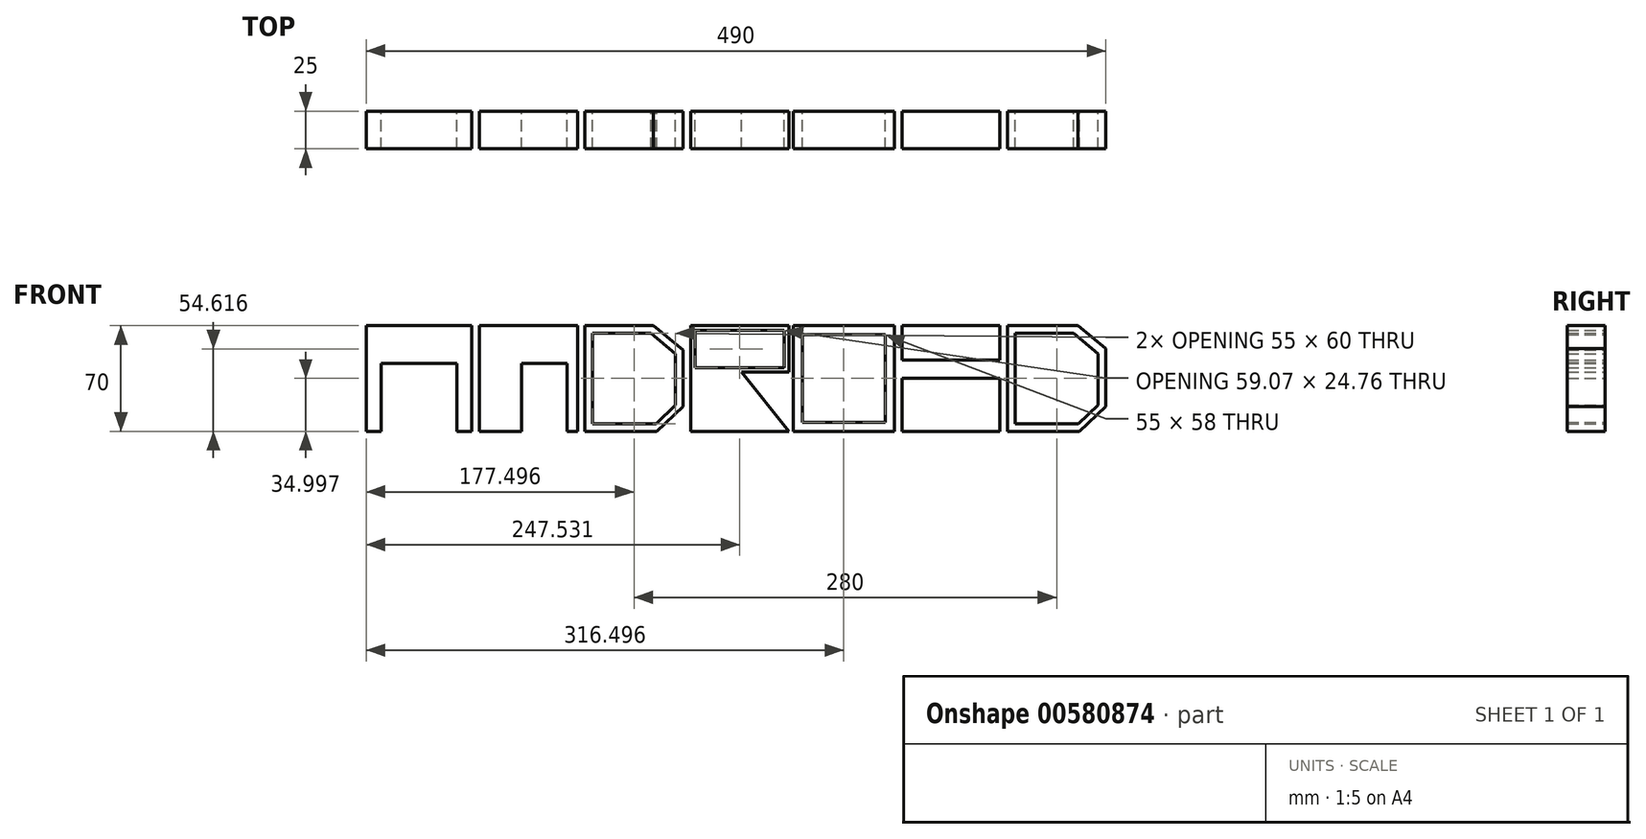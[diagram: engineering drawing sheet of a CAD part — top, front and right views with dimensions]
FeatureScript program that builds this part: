
annotation { "Feature Type Name" : "Feature", "Feature Type Description" : "" }
export const myFeature = defineFeature(function(context is Context, id is Id, definition is map)
    precondition{}
    {
        {
            var Q0;
            Q0=qCreatedBy(makeId("Front.planeOp"),FACE);
            var sketch = newSketch(context, id + "F0", { "sketchPlane" : qUnion([Q0])});
            skLineSegment(sketch, "E0.bottom", {"start": v(-253.98, -12.91) * mm, "end": v(-183.98, -12.91) * mm});
            skLineSegment(sketch, "E0.top", {"start": v(-253.98, -82.91) * mm, "end": v(-243.98, -82.91) * mm});
            skLineSegment(sketch, "E0.left", {"start": v(-253.98, -12.91) * mm, "end": v(-253.98, -82.91) * mm});
            skLineSegment(sketch, "E0.right", {"start": v(236.02, -28.1) * mm, "end": v(236.02, -66.45) * mm});
            skLineSegment(sketch, "E1.right", {"start": v(-183.98, -12.91) * mm, "end": v(-183.98, -82.91) * mm});
            skLineSegment(sketch, "E2.bottom", {"start": v(-178.98, -12.91) * mm, "end": v(-113.98, -12.91) * mm});
            skLineSegment(sketch, "E2.top", {"start": v(-178.98, -82.91) * mm, "end": v(-150.98, -82.91) * mm});
            skLineSegment(sketch, "E2.right", {"start": v(-113.98, -12.91) * mm, "end": v(-113.98, -82.91) * mm});
            skLineSegment(sketch, "E3.bottom", {"start": v(-108.98, -12.91) * mm, "end": v(-63.52, -12.91) * mm});
            skLineSegment(sketch, "E3.top", {"start": v(-108.98, -82.91) * mm, "end": v(-61.53, -82.91) * mm});
            skLineSegment(sketch, "E3.right", {"start": v(-43.98, -29.02) * mm, "end": v(-43.98, -66.45) * mm});
            skLineSegment(sketch, "E4.bottom", {"start": v(-38.98, -12.91) * mm, "end": v(26.02, -12.91) * mm});
            skLineSegment(sketch, "E4.top", {"start": v(-38.98, -82.91) * mm, "end": v(26.02, -82.91) * mm});
            skLineSegment(sketch, "E4.right", {"start": v(26.02, -12.91) * mm, "end": v(26.02, -43.67) * mm});
            skLineSegment(sketch, "E5.bottom", {"start": v(29.02, -12.91) * mm, "end": v(96.02, -12.91) * mm});
            skLineSegment(sketch, "E5.top", {"start": v(29.02, -82.91) * mm, "end": v(96.02, -82.91) * mm});
            skLineSegment(sketch, "E5.right", {"start": v(96.02, -12.91) * mm, "end": v(96.02, -82.91) * mm});
            skLineSegment(sketch, "E6.bottom", {"start": v(101.02, -12.91) * mm, "end": v(166.02, -12.91) * mm});
            skLineSegment(sketch, "E6.top", {"start": v(101.02, -82.91) * mm, "end": v(166.02, -82.91) * mm});
            skLineSegment(sketch, "E6.right", {"start": v(166.02, -12.91) * mm, "end": v(166.02, -35.66) * mm});
            skLineSegment(sketch, "E7", {"start": v(-243.98, -82.91) * mm, "end": v(-243.98, -37.91) * mm});
            skLineSegment(sketch, "E8", {"start": v(-243.98, -37.91) * mm, "end": v(-193.98, -37.91) * mm});
            skLineSegment(sketch, "E9", {"start": v(-193.98, -37.91) * mm, "end": v(-193.98, -82.91) * mm});
            skLineSegment(sketch, "E10", {"start": v(-193.98, -82.91) * mm, "end": v(-183.98, -82.91) * mm});
            skLineSegment(sketch, "E11.right", {"start": v(-178.98, -12.91) * mm, "end": v(-178.98, -82.91) * mm});
            skLineSegment(sketch, "E12.left", {"start": v(-178.98, -82.91) * mm, "end": v(-178.98, -82.91) * mm});
            skLineSegment(sketch, "E12.right", {"start": v(-150.98, -82.91) * mm, "end": v(-150.98, -82.91) * mm});
            skLineSegment(sketch, "E13.bottom", {"start": v(-150.98, -82.91) * mm, "end": v(-178.98, -82.91) * mm});
            skLineSegment(sketch, "E13.top", {"start": v(-150.98, -12.91) * mm, "end": v(-178.98, -12.91) * mm});
            skLineSegment(sketch, "E13.left", {"start": v(-150.98, -82.91) * mm, "end": v(-150.98, -37.91) * mm});
            skLineSegment(sketch, "E13.right", {"start": v(-178.98, -37.91) * mm, "end": v(-178.98, -12.91) * mm});
            skLineSegment(sketch, "E14.top", {"start": v(-150.98, -37.91) * mm, "end": v(-120.98, -37.91) * mm});
            skLineSegment(sketch, "E14.left", {"start": v(-178.98, -12.91) * mm, "end": v(-178.98, -37.91) * mm});
            skLineSegment(sketch, "E14.right", {"start": v(-113.98, -12.91) * mm, "end": v(-113.98, -37.91) * mm});
            skLineSegment(sketch, "E15.bottom", {"start": v(-113.98, -82.91) * mm, "end": v(-120.98, -82.91) * mm});
            skLineSegment(sketch, "E15.left", {"start": v(-113.98, -82.91) * mm, "end": v(-113.98, -38.68) * mm});
            skLineSegment(sketch, "E15.right", {"start": v(-120.98, -82.91) * mm, "end": v(-120.98, -37.91) * mm});
            skLineSegment(sketch, "E16.right", {"start": v(-108.98, -12.91) * mm, "end": v(-108.98, -82.91) * mm});
            skLineSegment(sketch, "E17", {"start": v(-43.98, -29.02) * mm, "end": v(-63.52, -12.91) * mm});
            skLineSegment(sketch, "E18", {"start": v(-103.98, -22.91) * mm, "end": v(-103.98, -77.91) * mm});
            skLineSegment(sketch, "E19", {"start": v(-61.9, -77.91) * mm, "end": v(-103.98, -77.91) * mm});
            skLineSegment(sketch, "E20", {"start": v(-48.98, -31.44) * mm, "end": v(-48.98, -24.9) * mm});
            skLineSegment(sketch, "E21", {"start": v(-103.98, -22.91) * mm, "end": v(-103.98, -17.91) * mm});
            skLineSegment(sketch, "E22", {"start": v(-48.98, -31.44) * mm, "end": v(-65.27, -17.91) * mm});
            skLineSegment(sketch, "E23", {"start": v(-103.98, -17.91) * mm, "end": v(-65.27, -17.91) * mm});
            skPoint(sketch, "E23.startSnap0", {"position": v(-103.98, -17.91) * mm});
            skLineSegment(sketch, "E24", {"start": v(-61.53, -82.91) * mm, "end": v(-43.98, -66.45) * mm});
            skLineSegment(sketch, "E25", {"start": v(-61.9, -77.91) * mm, "end": v(-48.98, -65.59) * mm});
            skPoint(sketch, "E26.orphan", {"position": v(-103.98, -12.91) * mm});
            skPoint(sketch, "E27.orphan", {"position": v(-108.98, -17.91) * mm});
            skLineSegment(sketch, "E28", {"start": v(-48.98, -31.44) * mm, "end": v(-48.98, -65.59) * mm});
            skLineSegment(sketch, "E29.right", {"start": v(-38.98, -12.91) * mm, "end": v(-38.98, -82.91) * mm});
            skLineSegment(sketch, "E30.left", {"start": v(-38.98, -12.91) * mm, "end": v(-38.98, -40.42) * mm});
            skLineSegment(sketch, "E30.right", {"start": v(26.02, -12.91) * mm, "end": v(26.02, -40.42) * mm});
            skLineSegment(sketch, "E31.top", {"start": v(-38.98, -82.91) * mm, "end": v(-5.14, -82.91) * mm});
            skLineSegment(sketch, "E31.left", {"start": v(-38.98, -40.42) * mm, "end": v(-38.98, -82.91) * mm});
            skLineSegment(sketch, "E32.bottom", {"start": v(-35.98, -15.91) * mm, "end": v(23.02, -15.91) * mm});
            skLineSegment(sketch, "E32.left", {"start": v(-35.98, -15.91) * mm, "end": v(-35.98, -37.42) * mm});
            skLineSegment(sketch, "E32.right", {"start": v(23.02, -15.91) * mm, "end": v(23.02, -37.42) * mm});
            skLineSegment(sketch, "E33", {"start": v(26.02, -82.91) * mm, "end": v(-5.4, -43.67) * mm});
            skLineSegment(sketch, "E34", {"start": v(-5.4, -43.67) * mm, "end": v(26.02, -43.67) * mm});
            skLineSegment(sketch, "E35", {"start": v(-35.98, -37.42) * mm, "end": v(-35.98, -40.67) * mm});
            skLineSegment(sketch, "E36", {"start": v(-35.98, -40.67) * mm, "end": v(23.09, -40.67) * mm});
            skLineSegment(sketch, "E37", {"start": v(23.09, -40.67) * mm, "end": v(23.02, -37.42) * mm});
            skLineSegment(sketch, "E38.right", {"start": v(29.02, -12.91) * mm, "end": v(29.02, -82.91) * mm});
            skLineSegment(sketch, "E39.bottom", {"start": v(35.02, -18.91) * mm, "end": v(90.02, -18.91) * mm});
            skLineSegment(sketch, "E39.top", {"start": v(35.02, -76.91) * mm, "end": v(90.02, -76.91) * mm});
            skLineSegment(sketch, "E39.left", {"start": v(35.02, -18.91) * mm, "end": v(35.02, -76.91) * mm});
            skLineSegment(sketch, "E39.right", {"start": v(90.02, -18.91) * mm, "end": v(90.02, -76.91) * mm});
            skLineSegment(sketch, "E40.right", {"start": v(101.02, -12.91) * mm, "end": v(101.02, -35.66) * mm});
            skLineSegment(sketch, "E41.top", {"start": v(101.02, -35.66) * mm, "end": v(166.02, -35.66) * mm});
            skLineSegment(sketch, "E42.bottom", {"start": v(166.02, -82.91) * mm, "end": v(101.02, -82.91) * mm});
            skLineSegment(sketch, "E42.top", {"start": v(166.02, -47.91) * mm, "end": v(101.02, -47.91) * mm});
            skLineSegment(sketch, "E42.left", {"start": v(166.02, -82.91) * mm, "end": v(166.02, -47.91) * mm});
            skLineSegment(sketch, "E42.right", {"start": v(101.02, -82.91) * mm, "end": v(101.02, -47.91) * mm});
            skLineSegment(sketch, "E43.right", {"start": v(171.02, -12.91) * mm, "end": v(171.02, -82.91) * mm});
            skLineSegment(sketch, "E44.bottom", {"start": v(171.02, -12.91) * mm, "end": v(217.61, -12.91) * mm});
            skLineSegment(sketch, "E45", {"start": v(176.02, -22.91) * mm, "end": v(176.02, -77.91) * mm});
            skLineSegment(sketch, "E46", {"start": v(218.1, -77.91) * mm, "end": v(176.02, -77.91) * mm});
            skLineSegment(sketch, "E47", {"start": v(176.02, -17.91) * mm, "end": v(214.73, -17.91) * mm});
            skLineSegment(sketch, "E48", {"start": v(218.47, -82.91) * mm, "end": v(236.02, -66.45) * mm});
            skLineSegment(sketch, "E49", {"start": v(218.1, -77.91) * mm, "end": v(231.02, -65.59) * mm});
            skLineSegment(sketch, "E50", {"start": v(231.02, -31.44) * mm, "end": v(231.02, -65.59) * mm});
            skLineSegment(sketch, "E51", {"start": v(176.02, -17.91) * mm, "end": v(176.02, -22.91) * mm});
            skLineSegment(sketch, "E52", {"start": v(214.73, -17.91) * mm, "end": v(231.02, -31.44) * mm});
            skLineSegment(sketch, "E53", {"start": v(236.02, -28.1) * mm, "end": v(217.61, -12.91) * mm});
            skLineSegment(sketch, "E54.trimOffspring", {"start": v(101.02, -47.91) * mm, "end": v(101.02, -82.91) * mm});
            skLineSegment(sketch, "E55.trimOffspring", {"start": v(166.02, -47.91) * mm, "end": v(166.02, -82.91) * mm});
            skLineSegment(sketch, "E56.trimOffspring", {"start": v(171.02, -82.91) * mm, "end": v(218.47, -82.91) * mm});
            skLineSegment(sketch, "E57.trimOffspring", {"start": v(-120.98, -82.91) * mm, "end": v(-113.98, -82.91) * mm});
            skSolve(sketch);
        }
        {
            var Q0;
            Q0 = qSketchRegion(id + "F0", true);
            extrude(context, id + "F1", {"entities" : qUnion([Q0]), "depth" : 25 * mm, "offsetDistance" : 25 * mm});
        }
    });
